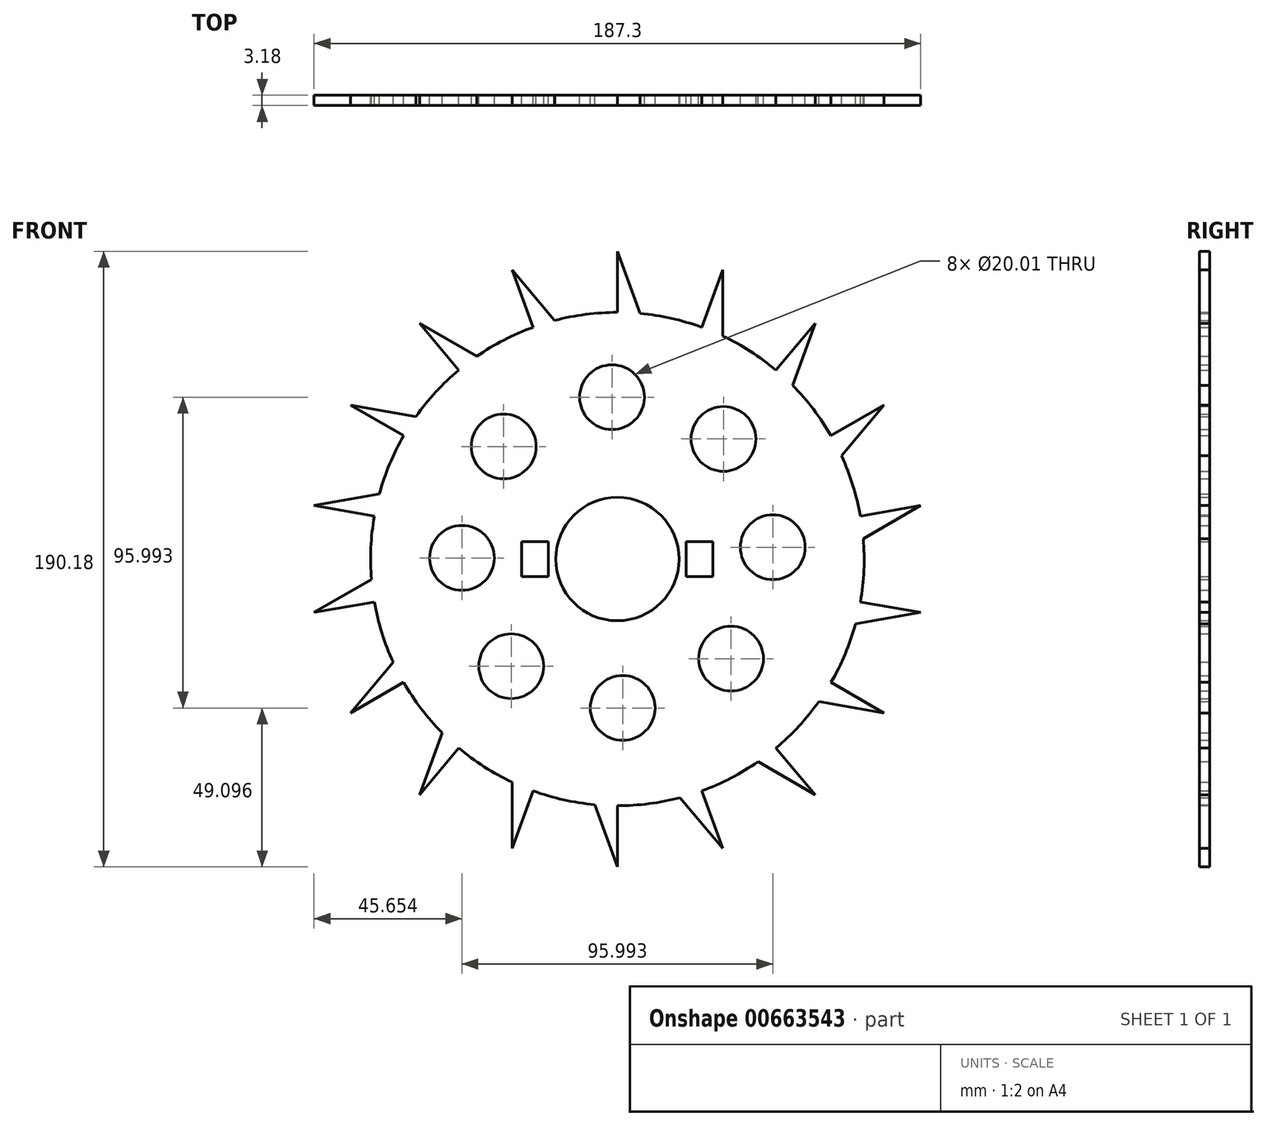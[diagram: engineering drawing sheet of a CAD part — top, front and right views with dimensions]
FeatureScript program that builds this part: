
annotation { "Feature Type Name" : "Feature", "Feature Type Description" : "" }
export const myFeature = defineFeature(function(context is Context, id is Id, definition is map)
    precondition{}
    {
        {
            var Q0;
            Q0=qCreatedBy(makeId("Front.planeOp"),FACE);
            var sketch = newSketch(context, id + "F0", { "sketchPlane" : qUnion([Q0])});
            skCircle(sketch, "E0", {"center": v(0, 0) * mm, "radius": 76.2 * mm});
            skLineSegment(sketch, "E1", {"start": v(0, 76.2) * mm, "end": v(0, 95.1) * mm});
            skLineSegment(sketch, "E2", {"start": v(0, 95.1) * mm, "end": v(7, 75.88) * mm});
            skLineSegment(sketch, "E3.1.0", {"start": v(32.52, 89.36) * mm, "end": v(32.52, 68.91) * mm});
            skLineSegment(sketch, "E3.1.1", {"start": v(26.06, 71.6) * mm, "end": v(32.52, 89.36) * mm});
            skLineSegment(sketch, "E3.2.0", {"start": v(61.12, 72.84) * mm, "end": v(54.13, 53.63) * mm});
            skLineSegment(sketch, "E3.2.1", {"start": v(48.98, 58.37) * mm, "end": v(61.12, 72.84) * mm});
            skLineSegment(sketch, "E3.3.0", {"start": v(82.35, 47.55) * mm, "end": v(69.2, 31.88) * mm});
            skLineSegment(sketch, "E3.3.1", {"start": v(66, 38.1) * mm, "end": v(82.35, 47.55) * mm});
            skLineSegment(sketch, "E3.4.0", {"start": v(93.65, 16.51) * mm, "end": v(75.94, 6.29) * mm});
            skLineSegment(sketch, "E3.4.1", {"start": v(75.04, 13.23) * mm, "end": v(93.65, 16.51) * mm});
            skLineSegment(sketch, "E3.5.0", {"start": v(93.65, -16.51) * mm, "end": v(73.51, -20.06) * mm});
            skLineSegment(sketch, "E3.5.1", {"start": v(75.04, -13.23) * mm, "end": v(93.65, -16.51) * mm});
            skLineSegment(sketch, "E3.6.0", {"start": v(82.35, -47.55) * mm, "end": v(62.22, -44) * mm});
            skLineSegment(sketch, "E3.6.1", {"start": v(66, -38.1) * mm, "end": v(82.35, -47.55) * mm});
            skLineSegment(sketch, "E3.7.0", {"start": v(61.12, -72.84) * mm, "end": v(43.42, -62.62) * mm});
            skLineSegment(sketch, "E3.7.1", {"start": v(48.98, -58.37) * mm, "end": v(61.12, -72.84) * mm});
            skLineSegment(sketch, "E3.8.0", {"start": v(32.52, -89.36) * mm, "end": v(19.38, -73.7) * mm});
            skLineSegment(sketch, "E3.8.1", {"start": v(26.06, -71.6) * mm, "end": v(32.52, -89.36) * mm});
            skLineSegment(sketch, "E3.9.0", {"start": v(0, -95.1) * mm, "end": v(-7, -75.88) * mm});
            skLineSegment(sketch, "E3.9.1", {"start": v(0, -76.2) * mm, "end": v(0, -95.1) * mm});
            skLineSegment(sketch, "E3.10.0", {"start": v(-32.52, -89.36) * mm, "end": v(-32.52, -68.91) * mm});
            skLineSegment(sketch, "E3.10.1", {"start": v(-26.06, -71.6) * mm, "end": v(-32.52, -89.36) * mm});
            skLineSegment(sketch, "E3.11.0", {"start": v(-61.12, -72.84) * mm, "end": v(-54.13, -53.63) * mm});
            skLineSegment(sketch, "E3.11.1", {"start": v(-48.98, -58.37) * mm, "end": v(-61.12, -72.84) * mm});
            skLineSegment(sketch, "E3.12.0", {"start": v(-82.35, -47.55) * mm, "end": v(-69.2, -31.88) * mm});
            skLineSegment(sketch, "E3.12.1", {"start": v(-66, -38.1) * mm, "end": v(-82.35, -47.55) * mm});
            skLineSegment(sketch, "E3.13.0", {"start": v(-93.65, -16.51) * mm, "end": v(-75.94, -6.29) * mm});
            skLineSegment(sketch, "E3.13.1", {"start": v(-75.04, -13.23) * mm, "end": v(-93.65, -16.51) * mm});
            skLineSegment(sketch, "E3.14.0", {"start": v(-93.65, 16.51) * mm, "end": v(-73.51, 20.06) * mm});
            skLineSegment(sketch, "E3.14.1", {"start": v(-75.04, 13.23) * mm, "end": v(-93.65, 16.51) * mm});
            skLineSegment(sketch, "E3.15.0", {"start": v(-82.35, 47.55) * mm, "end": v(-62.22, 44) * mm});
            skLineSegment(sketch, "E3.15.1", {"start": v(-66, 38.1) * mm, "end": v(-82.35, 47.55) * mm});
            skLineSegment(sketch, "E3.16.0", {"start": v(-61.12, 72.84) * mm, "end": v(-43.42, 62.62) * mm});
            skLineSegment(sketch, "E3.16.1", {"start": v(-48.98, 58.37) * mm, "end": v(-61.12, 72.84) * mm});
            skLineSegment(sketch, "E3.17.0", {"start": v(-32.52, 89.36) * mm, "end": v(-19.38, 73.7) * mm});
            skLineSegment(sketch, "E3.17.1", {"start": v(-26.06, 71.6) * mm, "end": v(-32.52, 89.36) * mm});
            skLineSegment(sketch, "E3.anchor1", {"start": v(0, 0) * mm, "end": v(7, 75.88) * mm, "construction": true});
            skLineSegment(sketch, "E3.anchor2", {"start": v(0, 0) * mm, "end": v(-19.38, 73.7) * mm, "construction": true});
            skCircle(sketch, "E4", {"center": v(0, 0) * mm, "radius": 19.05 * mm});
            skCircle(sketch, "E5", {"center": v(-48, 0.35) * mm, "radius": 10 * mm});
            skPoint(sketch, "E5.first.point", {"position": v(-58, 0) * mm});
            skPoint(sketch, "E5.second.point", {"position": v(-47.78, 10.35) * mm});
            skPoint(sketch, "E5.third.point", {"position": v(-38, 0) * mm});
            skCircle(sketch, "E6.1.0", {"center": v(-32.77, -33.1) * mm, "radius": 10 * mm});
            skCircle(sketch, "E6.2.0", {"center": v(1.65, -46) * mm, "radius": 10 * mm});
            skCircle(sketch, "E6.3.0", {"center": v(35.1, -30.77) * mm, "radius": 10 * mm});
            skCircle(sketch, "E6.4.0", {"center": v(48, 3.65) * mm, "radius": 10 * mm});
            skCircle(sketch, "E6.5.0", {"center": v(32.77, 37.1) * mm, "radius": 10 * mm});
            skCircle(sketch, "E6.6.0", {"center": v(-1.65, 50) * mm, "radius": 10 * mm});
            skCircle(sketch, "E6.7.0", {"center": v(-35.1, 34.77) * mm, "radius": 10 * mm});
            skPoint(sketch, "E6.center", {"position": v(0, 2) * mm});
            skLineSegment(sketch, "E7.bottom", {"start": v(-21.27, 5.44) * mm, "end": v(-29.53, 5.44) * mm});
            skLineSegment(sketch, "E7.top", {"start": v(-21.27, -5.44) * mm, "end": v(-29.53, -5.44) * mm});
            skLineSegment(sketch, "E7.left", {"start": v(-21.27, 5.44) * mm, "end": v(-21.27, -5.44) * mm});
            skLineSegment(sketch, "E7.right", {"start": v(-29.53, 5.44) * mm, "end": v(-29.53, -5.44) * mm});
            skPoint(sketch, "E7.middle", {"position": v(-25.4, 0) * mm});
            skLineSegment(sketch, "E8.2.0.0", {"start": v(29.53, 5.44) * mm, "end": v(21.27, 5.44) * mm});
            skLineSegment(sketch, "E8.2.0.1", {"start": v(29.53, -5.44) * mm, "end": v(21.27, -5.44) * mm});
            skLineSegment(sketch, "E8.2.0.2", {"start": v(21.27, 5.44) * mm, "end": v(21.27, -5.44) * mm});
            skLineSegment(sketch, "E8.2.0.3", {"start": v(29.53, 5.44) * mm, "end": v(29.53, -5.44) * mm});
            skLineSegment(sketch, "E8.direction1", {"start": v(-29.53, 5.44) * mm, "end": v(-4.13, 5.44) * mm, "construction": true});
            skSolve(sketch);
        }
        {
            var Q0;
            Q0 = qSketchRegion(id + "F0", true);
            extrude(context, id + "F1", {"entities" : qUnion([Q0]), "depth" : 3.17 * mm, "offsetDistance" : 25.4 * mm});
        }
    });
